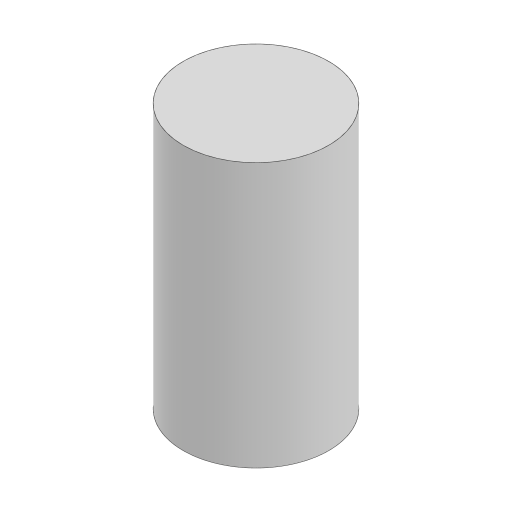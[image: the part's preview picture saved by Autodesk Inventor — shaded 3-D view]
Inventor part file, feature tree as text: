
AUTODESK INVENTOR PART (.ipt)
format: ipt  version: 2023 (Build 270158000, 158)  size: 81,920 bytes
history: native  units: in
note: dims shown in document units (in); Inventor stores cm internally (conversion verified against a paired STEP export)
features: other x1, extrude x1, sketch x1
ambient origin geometry x8: Origin, YZ Plane, XZ Plane, XY Plane, X Axis, Y Axis, Z Axis, Center Point
bodies: Body1 (feature_tree)
feature tree (3):
  other  "ソリッド1"
  extrude  "押し出し1"  Depth=2.5984in
  sketch  "スケッチ1"
